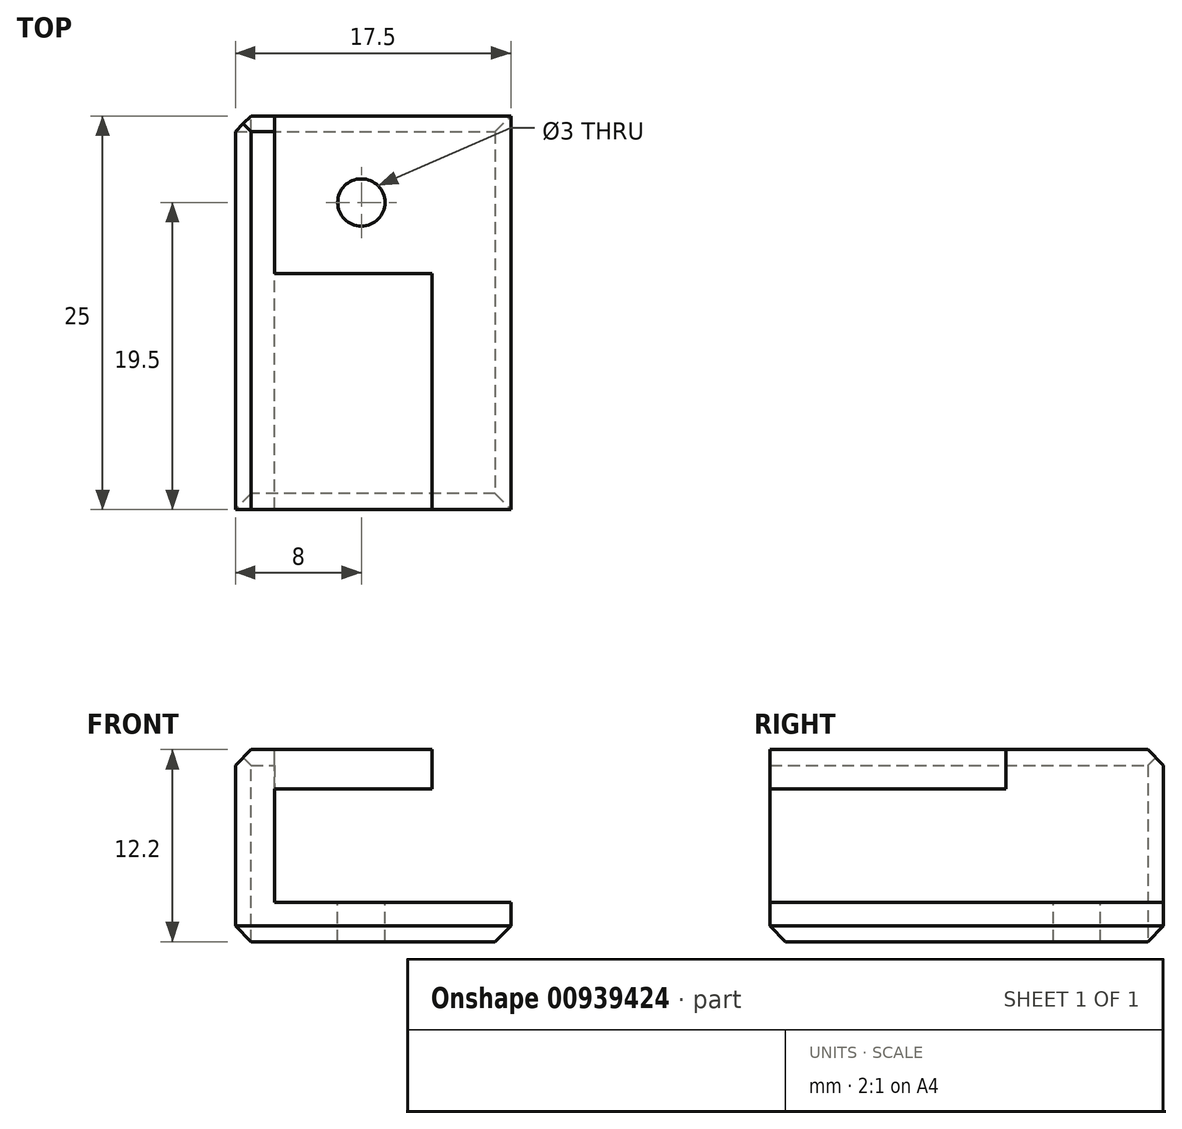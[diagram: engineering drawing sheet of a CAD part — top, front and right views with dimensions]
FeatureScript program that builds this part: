
annotation { "Feature Type Name" : "Feature", "Feature Type Description" : "" }
export const myFeature = defineFeature(function(context is Context, id is Id, definition is map)
    precondition{}
    {
        {
            var Q0;
            Q0=qCreatedBy(makeId("Front.planeOp"),FACE);
            var sketch = newSketch(context, id + "F0", { "sketchPlane" : qUnion([Q0])});
            skLineSegment(sketch, "E0", {"start": v(0, 3.6) * mm, "end": v(0, -3.6) * mm});
            skLineSegment(sketch, "E1", {"start": v(0, -3.6) * mm, "end": v(15, -3.6) * mm});
            skLineSegment(sketch, "E2", {"start": v(0, 3.6) * mm, "end": v(10, 3.6) * mm});
            skLineSegment(sketch, "E3.0", {"start": v(-2.5, -6.1) * mm, "end": v(15, -6.1) * mm});
            skLineSegment(sketch, "E3.1", {"start": v(-2.5, 6.1) * mm, "end": v(-2.5, -6.1) * mm});
            skLineSegment(sketch, "E3.2", {"start": v(-2.5, 6.1) * mm, "end": v(10, 6.1) * mm});
            skLineSegment(sketch, "E4", {"start": v(10, 6.1) * mm, "end": v(10, 3.6) * mm});
            skLineSegment(sketch, "E5", {"start": v(15, -3.6) * mm, "end": v(15, -6.1) * mm});
            skSolve(sketch);
        }
        {
            var Q0;
            Q0 = qSketchRegion(id + "F0", true);
            extrude(context, id + "F1", {"entities" : qUnion([Q0]), "depth" : 25 * mm, "offsetDistance" : 25 * mm});
        }
        {
            var Q0;
            Q0=makeQuery(id+"F1.opExtrude","SWEPT_FACE",FACE,{"disambiguationData":[OSD([sQuery(id+"F0.wireOp",EDGE,"E3.2")])]});
            var sketch = newSketch(context, id + "F2", { "sketchPlane" : qUnion([Q0])});
            skCircle(sketch, "E6", {"center": v(5.5, -5.5) * mm, "radius": 1.5 * mm});
            skSolve(sketch);
        }
        {
            var Q0;
            Q0=makeQuery(id+"F2.imprint","IMPRINT",FACE,{"disambiguationData":[TD([[makeQuery(id+"F2.imprint","IMPRINT",EDGE,{"derivedFrom":sQuery(id+"F2.wireOp",EDGE,"E6")}),1.0]])]});
            var Q1;
            Q1=sQuery(id+"F2.wireOp",EDGE,"E6");
            extrude(context, id + "F3", {"entities" : qUnion([Q0]), "operationType" : NewBodyOperationType.REMOVE, "surfaceEntities" : qUnion([Q1]), "oppositeDirection" : true, "depth" : 25 * mm, "offsetDistance" : 25 * mm});
        }
        {
            var Q0;
            Q0=makeQuery(id+"F1.opExtrude","SWEPT_FACE",FACE,{"disambiguationData":[OSD([sQuery(id+"F0.wireOp",EDGE,"E3.2")])]});
            var sketch = newSketch(context, id + "F4", { "sketchPlane" : qUnion([Q0])});
            skLineSegment(sketch, "E7", {"start": v(10, -10) * mm, "end": v(0, -10) * mm});
            skLineSegment(sketch, "E8", {"start": v(0, -10) * mm, "end": v(0, 0) * mm});
            skSolve(sketch);
        }
        {
            var Q0;
            Q0 = qSketchRegion(id + "F4", true);
            var Q1;
            {var subQ5=sQuery(id+"F4.wireOp",EDGE,"E7");Q1=makeQuery(id+"F4.imprint","IMPRINT",FACE,{"disambiguationData":[TD([[makeQuery(id+"F4.imprint","IMPRINT",EDGE,{"derivedFrom":subQ5}),-1.0]])]});}
            extrude(context, id + "F5", {"entities" : qUnion([Q0, Q1]), "operationType" : NewBodyOperationType.REMOVE, "oppositeDirection" : true, "depth" : 5 * mm, "offsetDistance" : 25 * mm});
        }
        {
            var Q0;
            Q0=makeQuery(id+"F1.opExtrude","SWEPT_EDGE",EDGE,{"disambiguationData":[OSD([sQuery(id+"F0.wireOp",EDGE,"E3.1"),sQuery(id+"F0.wireOp",EDGE,"E3.2")])]});
            var Q1;
            Q1=makeQuery(id+"F1.opExtrude","SWEPT_EDGE",EDGE,{"disambiguationData":[OSD([sQuery(id+"F0.wireOp",EDGE,"E3.0"),sQuery(id+"F0.wireOp",EDGE,"E3.1")])]});
            var Q2;
            Q2=makeQuery(id+"F1.opExtrude","SWEPT_EDGE",EDGE,{"disambiguationData":[OSD([sQuery(id+"F0.wireOp",EDGE,"E3.0"),sQuery(id+"F0.wireOp",EDGE,"E5")])]});
            var Q3;
            Q3=makeQuery(id+"F1.opExtrude","CAP_EDGE",EDGE,{"disambiguationData":[OSD([sQuery(id+"F0.wireOp",EDGE,"E3.0")])],"isStart":false});
            var Q4;
            Q4=makeQuery(id+"F1.opExtrude","CAP_EDGE",EDGE,{"disambiguationData":[OSD([sQuery(id+"F0.wireOp",EDGE,"E3.0")])],"isStart":true});
            var Q5;
            Q5=makeQuery(id+"F1.opExtrude","CAP_EDGE",EDGE,{"disambiguationData":[OSD([sQuery(id+"F0.wireOp",EDGE,"E3.1")])],"isStart":true});
            chamfer(context, id + "F6", {"entities" : qUnion([Q0, Q1, Q2, Q3, Q4, Q5]), "width" : 1 * mm, "tangentPropagation" : true});
        }
        {
            var Q0;
            Q0=makeQuery(id+"F1.opExtrude","CAP_EDGE",EDGE,{"disambiguationData":[OSD([sQuery(id+"F0.wireOp",EDGE,"E3.2")])],"isStart":true});
            chamfer(context, id + "F7", {"entities" : qUnion([Q0]), "width" : 1 * mm, "tangentPropagation" : true});
        }
    });
